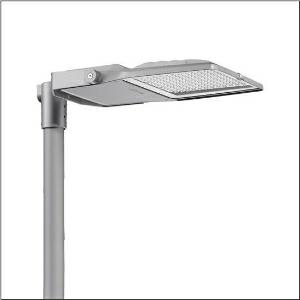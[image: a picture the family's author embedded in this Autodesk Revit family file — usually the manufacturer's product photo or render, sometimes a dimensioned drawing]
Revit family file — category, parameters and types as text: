
# Revit family: floodlight_fl_21_iq_midi___pl33t_5xa7781e4f3a_bb4e
name_source: partatom
category: Lighting Fixtures
units: mm (PartAtom-declared; Revit-internal decimal feet)

## family parameters
Cut with Voids When Loaded = No
Host = Face
Light Source = No
Part Type = Normal
Room Calculation Point = No
Round Connector Dimension = Use Diameter
Shared = No

## types (1)
- --- (1 x LED, 27690 lm, 208.1 W, 4000K)
    Apparent Load = 208 VA
    CIE Flux Codes = 26 75 99 100 100
    Color Rendering = 70
    Color Temperature = 4000K
    Default Elevation = 1800 mm
    Description = Floodlight FL 21 iQ midi, floodlight, primary light control with lens, of PMMA, primary optical cover: protective disc, of toughened safety glass, transparent, light distribution: PL33T, light emission: direct distribution, installation type: surface-mounted, LED, High Power LED, rated luminous flux: 27.690lm, luminous efficacy: 133lm/W, light colour: 740, colour temperature: 4000K, control gear: iQ Comfort/DALI, control: optimised constant luminous flux control (CLO 2.0), Desk-Remote (wireless, voltage-free reading and setting of iQ features in the workshop via application-optimized NFC function/RFID function), Light-Fading, Smart-Wire, Night-Set, Lumen-Switch, Temp-Guard, Auto-Match, with terminal, 6-pole, mains connection: 220..240V, AC, 50/60Hz, start of lifetime: 208W, end of service life: 227W, reduction: 90W, luminaire housing, of diecast aluminium, powder-coated, Siteco® metallic grey (DB 702S), corrosivity category C5 mid according to DIN EN ISO 12944, suitable for swimming pools, chlorine-resistant, sealing non-destructively replaceable, please order mast flange separately, mast bracket, of steel, galvanised, powder-coated, Siteco® metallic grey (DB 702S), protection rating (complete): IP66, insulation class (complete): insulation class II (safety insulation), certification: CE, ENEC, VDE, protection symbol: D, impact resistance: IK08, permissible operating ambient temperature: -40..+40°C, permissible operating ambient temperature for outdoor applications: -40..+50°C, standard: DIN EN 12944, LABS conformity tested according to VDMA 24364:2018-05, packaging unit: 1 piece

Light Distribution: PL33T
    Height = 76 mm
    Lamp = 1 x LED
    Lamp Light Flux = 27690 lm
    Lamp Power = 208.1 W
    Lamp count = 1
    Length = 657 mm
    Luminous efficacy = 133 lm/W
    Manufacturer = Siteco
    ModVariant = No
    Model = 5XA7781E4F3A
    Number of Poles = 1
    OnlyDefault = Yes
    Power Factor = 1
    Product Name = Floodlight FL 21 iQ midi | PL33T
    Product group = floodlight | pylon annexe
    ProductGroupID = 6200
    Protection Class = Protection class II
    Protection Degree = IP 66
    RLX_Detail_Level = 1
    RLX_Emergency_Light_Flux = 0 lm
    RLX_Emergency_Type = 0
    RLX_Emergency_Type_DB = No
    RlxData = <blob elided: 153817 chars, md5=c31655b8>
    Socket = socket
    Standby Power = 0 W
    System Light Flux = 27690 lm
    System Power = 208 W
    Type Comments = factory setting: luminous flux: 100 % | dim-lin: 254 | 710 mA
    Type Image = l_1007123.jpg
    URL = http://relux.com
    VarID = @adj_103944
    Voltage = 0 V
    Weight = 0.00 kg
    Width = 442 mm

## geometry (parser evidence)
native form markers: Blend x4, Sweep x12
no freeform markers — native parametric forms only
